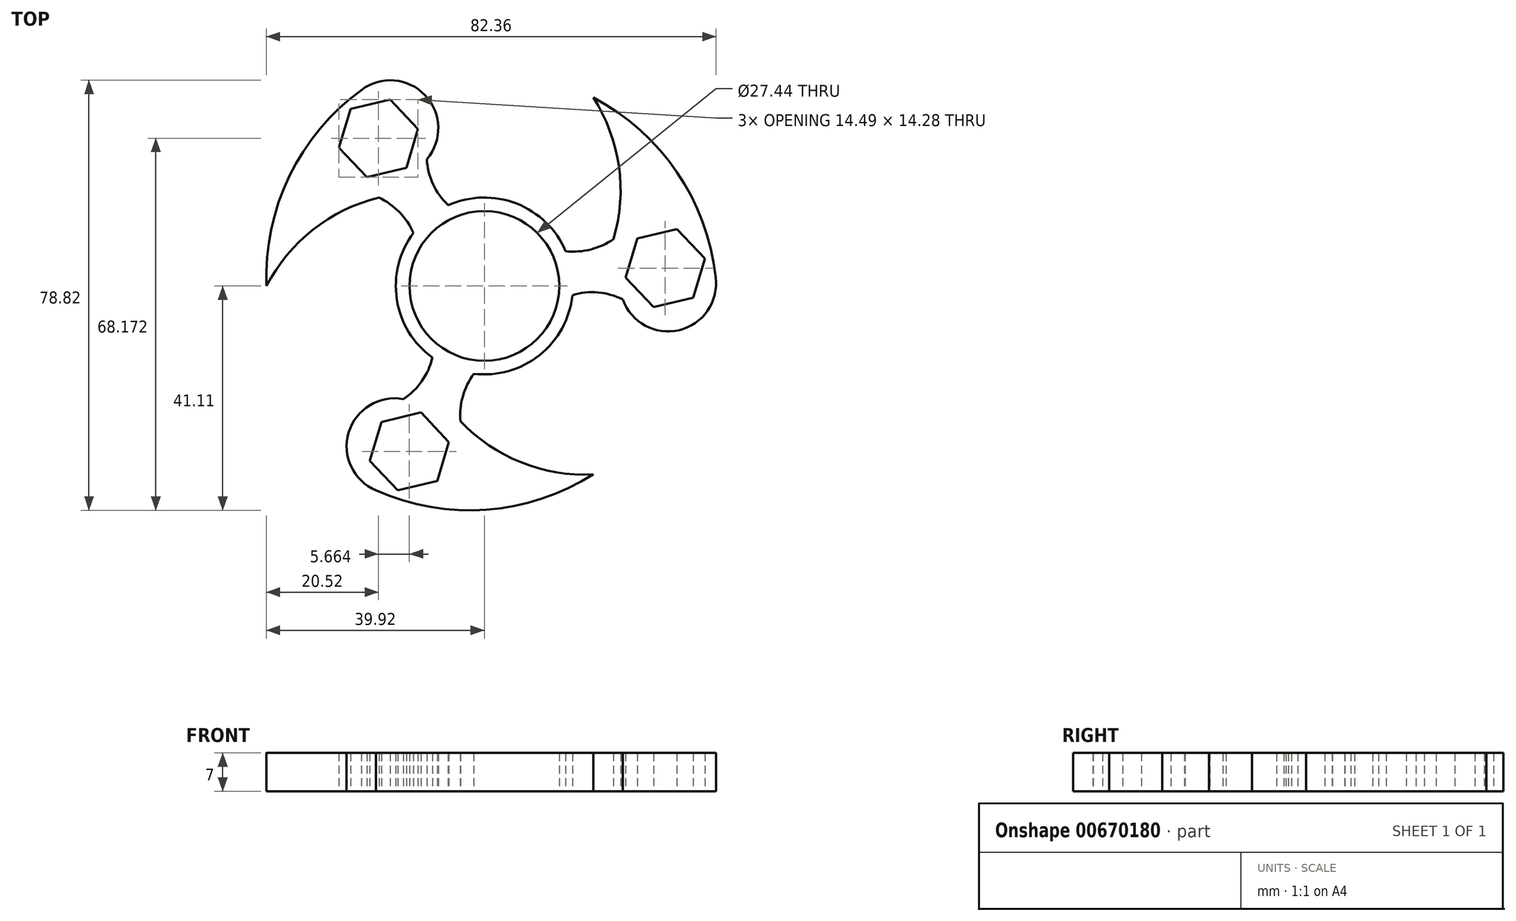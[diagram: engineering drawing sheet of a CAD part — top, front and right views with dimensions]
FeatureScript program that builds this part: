
annotation { "Feature Type Name" : "Feature", "Feature Type Description" : "" }
export const myFeature = defineFeature(function(context is Context, id is Id, definition is map)
    precondition{}
    {
        {
            var Q0;
            Q0=qCreatedBy(makeId("Top.planeOp"),FACE);
            var sketch = newSketch(context, id + "F0", { "sketchPlane" : qUnion([Q0])});
            skCircle(sketch, "E0", {"center": v(0, 0) * mm, "radius": 13.72 * mm});
            skCircle(sketch, "E1", {"center": v(0, 0) * mm, "radius": 16.22 * mm});
            skArc(sketch, "E2", {"start": v(-10.54, 23.22) * mm, "mid": v(-9.24, 18.33) * mm, "end": v(-6.1, 14.35) * mm});
            skArc(sketch, "E3", {"start": v(-12.7, 9.05) * mm, "mid": v(-15.3, 13.27) * mm, "end": v(-19.3, 16.2) * mm});
            skArc(sketch, "E4", {"start": v(-10.54, 23.22) * mm, "mid": v(-10.84, 34.96) * mm, "end": v(-22.54, 35.9) * mm});
            skArc(sketch, "E5", {"start": v(-22.54, 35.9) * mm, "mid": v(-35.72, 20.13) * mm, "end": v(-39.89, 0) * mm});
            skArc(sketch, "E6", {"start": v(-19.3, 16.2) * mm, "mid": v(-31.36, 10.34) * mm, "end": v(-39.89, 0) * mm});
            skArc(sketch, "E7.1.0", {"start": v(25.38, -2.48) * mm, "mid": v(20.5, -1.16) * mm, "end": v(15.48, -1.9) * mm});
            skArc(sketch, "E7.1.1", {"start": v(25.38, -2.48) * mm, "mid": v(35.7, -8.1) * mm, "end": v(42.37, 1.57) * mm});
            skArc(sketch, "E7.1.2", {"start": v(42.37, 1.57) * mm, "mid": v(35.3, 20.87) * mm, "end": v(19.94, 34.54) * mm});
            skArc(sketch, "E7.1.3", {"start": v(23.68, 8.61) * mm, "mid": v(24.63, 21.99) * mm, "end": v(19.94, 34.54) * mm});
            skArc(sketch, "E7.1.4", {"start": v(14.19, 6.47) * mm, "mid": v(19.14, 6.62) * mm, "end": v(23.68, 8.61) * mm});
            skArc(sketch, "E7.2.0", {"start": v(-14.84, -20.74) * mm, "mid": v(-11.25, -17.16) * mm, "end": v(-9.38, -12.46) * mm});
            skArc(sketch, "E7.2.1", {"start": v(-14.84, -20.74) * mm, "mid": v(-24.85, -26.87) * mm, "end": v(-19.83, -37.48) * mm});
            skArc(sketch, "E7.2.2", {"start": v(-19.83, -37.48) * mm, "mid": v(0.43, -41) * mm, "end": v(19.94, -34.54) * mm});
            skArc(sketch, "E7.2.3", {"start": v(-4.38, -24.81) * mm, "mid": v(6.72, -32.33) * mm, "end": v(19.94, -34.54) * mm});
            skArc(sketch, "E7.2.4", {"start": v(-1.49, -15.52) * mm, "mid": v(-3.84, -19.88) * mm, "end": v(-4.38, -24.81) * mm});
            skLineSegment(sketch, "E8.0", {"start": v(-17.27, 34.2) * mm, "end": v(-12.16, 28.79) * mm});
            skLineSegment(sketch, "E8.1", {"start": v(-12.16, 28.79) * mm, "end": v(-14.28, 21.65) * mm});
            skLineSegment(sketch, "E8.2", {"start": v(-14.28, 21.65) * mm, "end": v(-21.53, 19.92) * mm});
            skLineSegment(sketch, "E8.3", {"start": v(-21.53, 19.92) * mm, "end": v(-26.65, 25.34) * mm});
            skLineSegment(sketch, "E8.4", {"start": v(-26.65, 25.34) * mm, "end": v(-24.52, 32.47) * mm});
            skLineSegment(sketch, "E8.5", {"start": v(-24.52, 32.47) * mm, "end": v(-17.27, 34.2) * mm});
            skLineSegment(sketch, "E9.1.0", {"start": v(-15.86, -37.47) * mm, "end": v(-20.98, -32.06) * mm});
            skLineSegment(sketch, "E9.1.1", {"start": v(-20.98, -32.06) * mm, "end": v(-18.85, -24.92) * mm});
            skLineSegment(sketch, "E9.1.2", {"start": v(-18.85, -24.92) * mm, "end": v(-11.6, -23.2) * mm});
            skLineSegment(sketch, "E9.1.3", {"start": v(-11.6, -23.2) * mm, "end": v(-6.5, -28.6) * mm});
            skLineSegment(sketch, "E9.1.4", {"start": v(-6.5, -28.6) * mm, "end": v(-8.62, -35.74) * mm});
            skLineSegment(sketch, "E9.1.5", {"start": v(-8.62, -35.74) * mm, "end": v(-15.86, -37.47) * mm});
            skLineSegment(sketch, "E9.2.0", {"start": v(40.38, 5) * mm, "end": v(38.25, -2.14) * mm});
            skLineSegment(sketch, "E9.2.1", {"start": v(38.25, -2.14) * mm, "end": v(31.01, -3.87) * mm});
            skLineSegment(sketch, "E9.2.2", {"start": v(31.01, -3.87) * mm, "end": v(25.9, 1.54) * mm});
            skLineSegment(sketch, "E9.2.3", {"start": v(25.9, 1.54) * mm, "end": v(28.02, 8.68) * mm});
            skLineSegment(sketch, "E9.2.4", {"start": v(28.02, 8.68) * mm, "end": v(35.26, 10.4) * mm});
            skLineSegment(sketch, "E9.2.5", {"start": v(35.26, 10.4) * mm, "end": v(40.38, 5) * mm});
            skSolve(sketch);
        }
        {
            var Q0;
            {var subQ0=sQuery(id+"F0.wireOp",EDGE,"E7.1.0");Q0=makeQuery(id+"F0.imprint","IMPRINT",FACE,{"disambiguationData":[TD([[makeQuery(id+"F0.imprint","IMPRINT",EDGE,{"derivedFrom":subQ0}),-1.0]])]});}
            var Q1;
            {var subQ0=sQuery(id+"F0.wireOp",EDGE,"f908f89b-4516-46d8-bc86-c1e72a5e4694.8");Q1=makeQuery(id+"F0.imprint","IMPRINT",FACE,{"disambiguationData":[TD([[makeQuery(id+"F0.imprint","IMPRINT",EDGE,{"derivedFrom":subQ0}),1.0]])]});}
            var Q2;
            {var subQ0=sQuery(id+"F0.wireOp",EDGE,"f908f89b-4516-46d8-bc86-c1e72a5e4694.7");Q2=makeQuery(id+"F0.imprint","IMPRINT",FACE,{"disambiguationData":[TD([[makeQuery(id+"F0.imprint","IMPRINT",EDGE,{"derivedFrom":subQ0}),1.0]])]});}
            var Q3;
            {var subQ0=sQuery(id+"F0.wireOp",EDGE,"f908f89b-4516-46d8-bc86-c1e72a5e4694.6");Q3=makeQuery(id+"F0.imprint","IMPRINT",FACE,{"disambiguationData":[TD([[makeQuery(id+"F0.imprint","IMPRINT",EDGE,{"derivedFrom":subQ0}),1.0]])]});}
            var Q4;
            {var subQ0=sQuery(id+"F0.wireOp",EDGE,"f908f89b-4516-46d8-bc86-c1e72a5e4694.5");Q4=makeQuery(id+"F0.imprint","IMPRINT",FACE,{"disambiguationData":[TD([[makeQuery(id+"F0.imprint","IMPRINT",EDGE,{"derivedFrom":subQ0}),1.0]])]});}
            var Q5;
            {var subQ0=sQuery(id+"F0.wireOp",EDGE,"f908f89b-4516-46d8-bc86-c1e72a5e4694.4");Q5=makeQuery(id+"F0.imprint","IMPRINT",FACE,{"disambiguationData":[TD([[makeQuery(id+"F0.imprint","IMPRINT",EDGE,{"derivedFrom":subQ0}),1.0]])]});}
            var Q6;
            {var subQ0=sQuery(id+"F0.wireOp",EDGE,"f908f89b-4516-46d8-bc86-c1e72a5e4694.3");Q6=makeQuery(id+"F0.imprint","IMPRINT",FACE,{"disambiguationData":[TD([[makeQuery(id+"F0.imprint","IMPRINT",EDGE,{"derivedFrom":subQ0}),1.0]])]});}
            var Q7;
            Q7=makeQuery(id+"F0.imprint","IMPRINT",FACE,{"disambiguationData":[TD([[makeQuery(id+"F0.imprint","IMPRINT",EDGE,{"derivedFrom":sQuery(id+"F0.wireOp",EDGE,"E0")}),-1.0]])]});
            var Q8;
            {var subQ0=sQuery(id+"F0.wireOp",EDGE,"f908f89b-4516-46d8-bc86-c1e72a5e4694.0");Q8=makeQuery(id+"F0.imprint","IMPRINT",FACE,{"disambiguationData":[TD([[makeQuery(id+"F0.imprint","IMPRINT",EDGE,{"derivedFrom":subQ0}),1.0]])]});}
            var Q9;
            {var subQ0=sQuery(id+"F0.wireOp",EDGE,"f908f89b-4516-46d8-bc86-c1e72a5e4694.1");Q9=makeQuery(id+"F0.imprint","IMPRINT",FACE,{"disambiguationData":[TD([[makeQuery(id+"F0.imprint","IMPRINT",EDGE,{"derivedFrom":subQ0}),1.0]])]});}
            var Q10;
            {var subQ0=sQuery(id+"F0.wireOp",EDGE,"f908f89b-4516-46d8-bc86-c1e72a5e4694.2");Q10=makeQuery(id+"F0.imprint","IMPRINT",FACE,{"disambiguationData":[TD([[makeQuery(id+"F0.imprint","IMPRINT",EDGE,{"derivedFrom":subQ0}),1.0]])]});}
            var Q11;
            {var subQ0=sQuery(id+"F0.wireOp",EDGE,"E7.2.0");Q11=makeQuery(id+"F0.imprint","IMPRINT",FACE,{"disambiguationData":[TD([[makeQuery(id+"F0.imprint","IMPRINT",EDGE,{"derivedFrom":subQ0}),-1.0]])]});}
            var Q12;
            {var subQ1=sQuery(id+"F0.wireOp",EDGE,"E2");Q12=makeQuery(id+"F0.imprint","IMPRINT",FACE,{"disambiguationData":[TD([[makeQuery(id+"F0.imprint","IMPRINT",EDGE,{"derivedFrom":subQ1}),-1.0]])]});}
            extrude(context, id + "F1", {"entities" : qUnion([Q0, Q1, Q2, Q3, Q4, Q5, Q6, Q7, Q8, Q9, Q10, Q11, Q12]), "depth" : 7 * mm, "offsetDistance" : 25 * mm});
        }
    });
